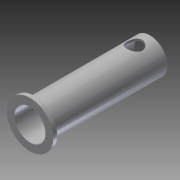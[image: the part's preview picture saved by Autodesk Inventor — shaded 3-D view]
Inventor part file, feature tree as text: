
AUTODESK INVENTOR PART (.ipt)
format: ipt  version: 2013 (Build 170138000, 138)  size: 110,080 bytes
history: native  units: in
note: dims shown in document units (in); Inventor stores cm internally (conversion verified against a paired STEP export)
features: extrude x3, sketch x3, plane x2
ambient origin geometry x8: Origin, YZ Plane, XZ Plane, XY Plane, X Axis, Y Axis, Z Axis, Center Point
bodies: Solid1 (feature_tree)
feature tree (8):
  extrude  "Extrusion1"  Depth=0.4in
  extrude  "Extrusion2"  Depth=0.6in
  plane  "Work Plane2"
  extrude  "Extrusion3"  Depth=0.25in TaperAngle=90.0deg
  sketch  "Sketch1"  dims[d0=0.45in d1=0.4in]
  sketch  "Sketch2"  dims[d2=1.5in d3=0.0in d4=0.6in]
  plane  "Work Plane1"
  sketch  "Sketch3"  dims[d5=0.05in d6=0.0in d7=90.0deg d8=0.25in d9=0.2in d10=0.2in d11=1.0in d12=0.0in]
